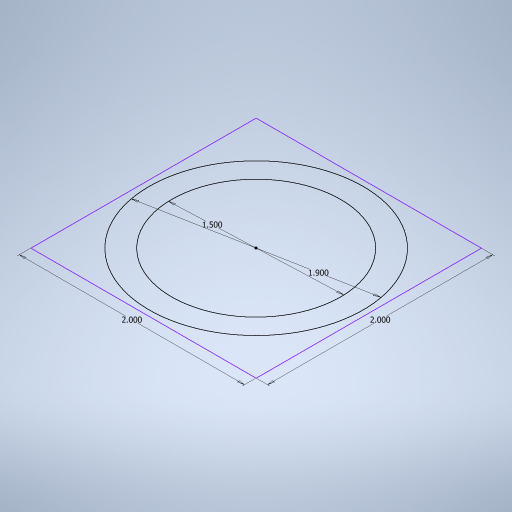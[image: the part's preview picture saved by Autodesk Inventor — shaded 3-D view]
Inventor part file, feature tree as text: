
AUTODESK INVENTOR PART (.ipt)
format: ipt  version: 2023 (Build 270158000, 158)  size: 237,568 bytes
history: native  units: in
note: dims shown in document units (in); Inventor stores cm internally (conversion verified against a paired STEP export)
features: sketch x1
ambient origin geometry x8: Origin, YZ Plane, XZ Plane, XY Plane, X Axis, Y Axis, Z Axis, Center Point
feature tree (1):
  sketch  "Sketch1"  dims[d0=1.5in d1=1.9in d4=2.0in d5=2.0in]
